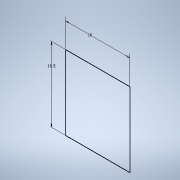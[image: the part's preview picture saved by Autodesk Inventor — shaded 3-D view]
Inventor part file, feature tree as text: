
AUTODESK INVENTOR PART (.ipt)
format: ipt  version: 2021 (Build 250183000, 183)  size: 87,040 bytes
history: native  units: mm
features: sketch x1
ambient origin geometry x8: Origin, YZ Plane, XZ Plane, XY Plane, X Axis, Y Axis, Z Axis, Center Point
feature tree (1):
  sketch  "Skizze1"  dims[d0=16.0mm d1=18.5mm]
